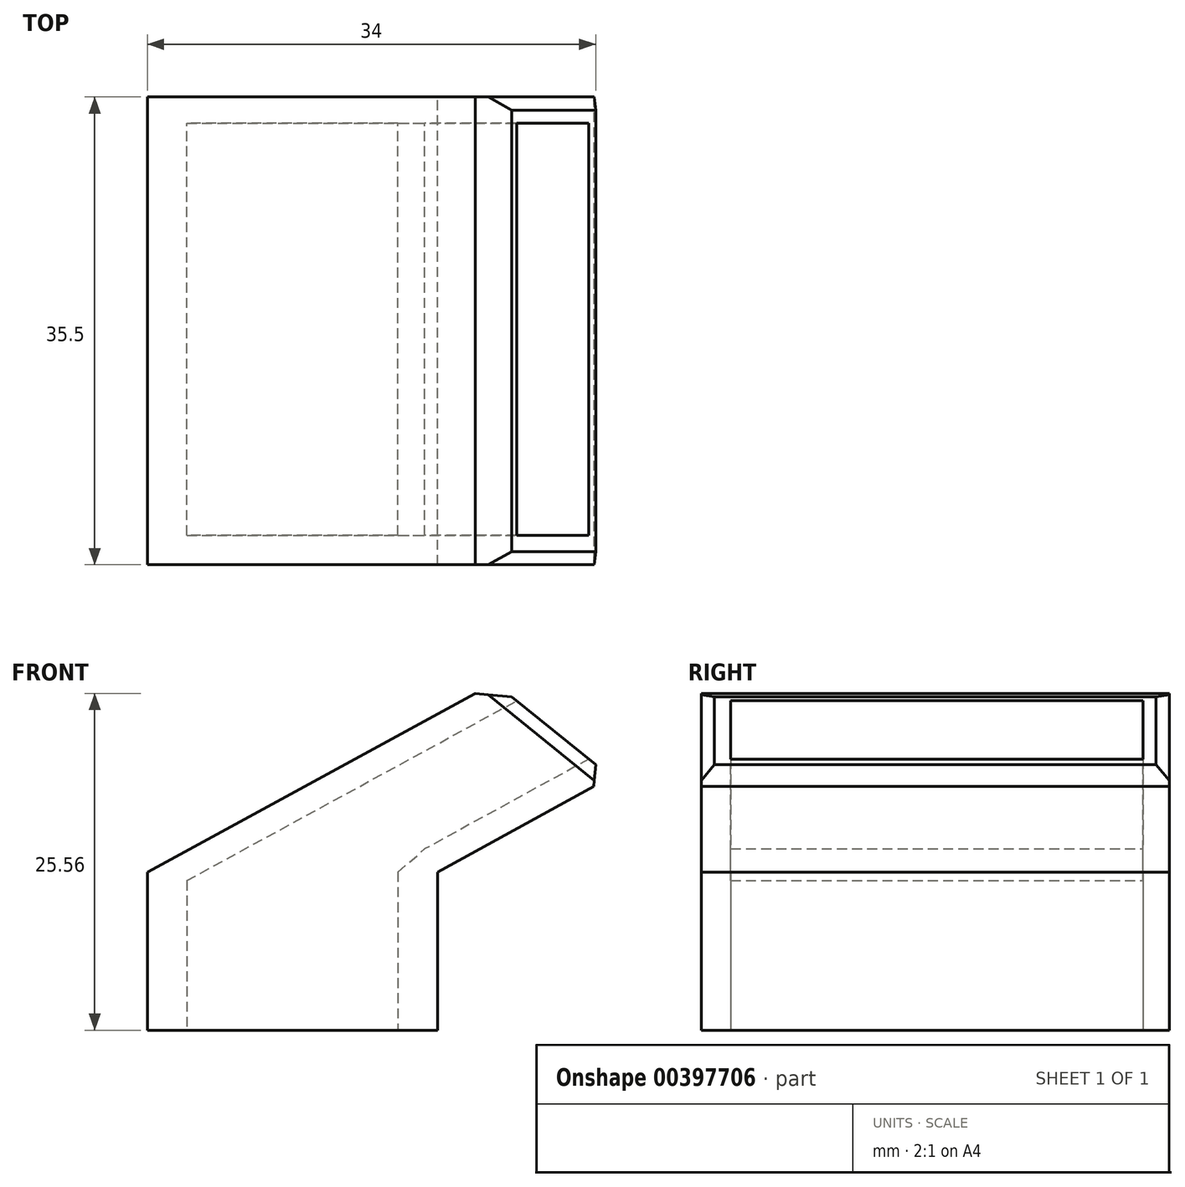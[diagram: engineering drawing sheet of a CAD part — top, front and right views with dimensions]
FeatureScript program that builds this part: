
annotation { "Feature Type Name" : "Feature", "Feature Type Description" : "" }
export const myFeature = defineFeature(function(context is Context, id is Id, definition is map)
    precondition{}
    {
        {
            var Q0;
            Q0=qCreatedBy(makeId("Front.planeOp"),FACE);
            var sketch = newSketch(context, id + "F0", { "sketchPlane" : qUnion([Q0])});
            skLineSegment(sketch, "E0.bottom", {"start": v(11, 6) * mm, "end": v(-11, 6) * mm});
            skLineSegment(sketch, "E0.top", {"start": v(11, -6) * mm, "end": v(-11, -6) * mm});
            skLineSegment(sketch, "E0.left", {"start": v(11, 6) * mm, "end": v(11, -6) * mm});
            skLineSegment(sketch, "E0.right", {"start": v(-11, 6) * mm, "end": v(-11, -6) * mm});
            skPoint(sketch, "E0.middle", {"position": v(0, 0) * mm});
            skLineSegment(sketch, "E1", {"start": v(-11, 6) * mm, "end": v(15.34, 20.36) * mm});
            skLineSegment(sketch, "E2", {"start": v(15.34, 20.36) * mm, "end": v(24.16, 13.2) * mm});
            skLineSegment(sketch, "E3", {"start": v(24.16, 13.2) * mm, "end": v(11, 6) * mm});
            skLineSegment(sketch, "E4.0", {"start": v(8, 6) * mm, "end": v(8, -6) * mm});
            skLineSegment(sketch, "E5.0", {"start": v(22.48, 14.57) * mm, "end": v(10.04, 7.75) * mm});
            skLineSegment(sketch, "E6.0", {"start": v(-8, 5.36) * mm, "end": v(16.3, 18.6) * mm});
            skLineSegment(sketch, "E7.0", {"start": v(-8, 5.36) * mm, "end": v(-8, -6) * mm});
            skLineSegment(sketch, "E8", {"start": v(8, 6) * mm, "end": v(10.04, 7.75) * mm});
            skLineSegment(sketch, "E9", {"start": v(16.3, 18.6) * mm, "end": v(17.02, 19) * mm});
            skSolve(sketch);
        }
        {
            var Q0;
            {var subQ0=sQuery(id+"F0.wireOp",EDGE,"E0.left");Q0=makeQuery(id+"F0.imprint","IMPRINT",FACE,{"disambiguationData":[TD([[makeQuery(id+"F0.imprint","IMPRINT",EDGE,{"derivedFrom":subQ0}),-1.0]])]});}
            var Q1;
            {var subQ4=sQuery(id+"F0.wireOp",EDGE,"E4.0");Q1=makeQuery(id+"F0.imprint","IMPRINT",FACE,{"disambiguationData":[TD([[makeQuery(id+"F0.imprint","IMPRINT",EDGE,{"derivedFrom":subQ4}),-1.0]])]});}
            var Q2;
            {var subQ1=sQuery(id+"F0.wireOp",EDGE,"E3");Q2=makeQuery(id+"F0.imprint","IMPRINT",FACE,{"disambiguationData":[TD([[makeQuery(id+"F0.imprint","IMPRINT",EDGE,{"derivedFrom":subQ1}),-1.0]])]});}
            var Q3;
            {var subQ0=sQuery(id+"F0.wireOp",EDGE,"E5.0");Q3=makeQuery(id+"F0.imprint","IMPRINT",FACE,{"disambiguationData":[TD([[makeQuery(id+"F0.imprint","IMPRINT",EDGE,{"derivedFrom":subQ0}),-1.0]])]});}
            var Q4;
            {var subQ5=sQuery(id+"F0.wireOp",EDGE,"E1");Q4=makeQuery(id+"F0.imprint","IMPRINT",FACE,{"disambiguationData":[TD([[makeQuery(id+"F0.imprint","IMPRINT",EDGE,{"derivedFrom":subQ5}),-1.0]])]});}
            var Q5;
            {var subQ4=sQuery(id+"F0.wireOp",EDGE,"E0.right");Q5=makeQuery(id+"F0.imprint","IMPRINT",FACE,{"disambiguationData":[TD([[makeQuery(id+"F0.imprint","IMPRINT",EDGE,{"derivedFrom":subQ4}),1.0]])]});}
            extrude(context, id + "F1", {"entities" : qUnion([Q0, Q1, Q2, Q3, Q4, Q5]), "depth" : 35.5 * mm});
        }
        {
            var Q0;
            {var subQ4=sQuery(id+"F0.wireOp",EDGE,"E4.0");Q0=makeQuery(id+"F0.imprint","IMPRINT",FACE,{"disambiguationData":[TD([[makeQuery(id+"F0.imprint","IMPRINT",EDGE,{"derivedFrom":subQ4}),-1.0]])]});}
            var Q1;
            {var subQ0=sQuery(id+"F0.wireOp",EDGE,"E5.0");Q1=makeQuery(id+"F0.imprint","IMPRINT",FACE,{"disambiguationData":[TD([[makeQuery(id+"F0.imprint","IMPRINT",EDGE,{"derivedFrom":subQ0}),-1.0]])]});}
            extrude(context, id + "F2", {"entities" : qUnion([Q0, Q1]), "operationType" : NewBodyOperationType.REMOVE, "depth" : 33.25 * mm, "hasSecondDirection" : true, "secondDirectionOppositeDirection" : false, "secondDirectionDepth" : 2 * mm});
        }
        {
            var Q0;
            Q0=makeQuery(id+"F1.opExtrude","SWEPT_EDGE",EDGE,{"disambiguationData":[OSD([sQuery(id+"F0.wireOp",EDGE,"E1"),sQuery(id+"F0.wireOp",EDGE,"E2")])]});
            chamfer(context, id + "F3", {"entities" : qUnion([Q0]), "width" : 2.5 * mm, "tangentPropagation" : true});
        }
        {
            var Q0;
            Q0=makeQuery(id+"F1.opExtrude","SWEPT_EDGE",EDGE,{"disambiguationData":[OSD([sQuery(id+"F0.wireOp",EDGE,"E2"),sQuery(id+"F0.wireOp",EDGE,"E3")])]});
            var Q1;
            Q1=makeQuery(id+"F1.opExtrude","CAP_EDGE",EDGE,{"disambiguationData":[OSD([sQuery(id+"F0.wireOp",EDGE,"E2")])],"isStart":false});
            var Q2;
            Q2=makeQuery(id+"F1.opExtrude","CAP_EDGE",EDGE,{"disambiguationData":[OSD([sQuery(id+"F0.wireOp",EDGE,"E2")])],"isStart":true});
            chamfer(context, id + "F4", {"entities" : qUnion([Q0, Q1, Q2]), "width" : 1 * mm, "tangentPropagation" : true});
        }
    });
